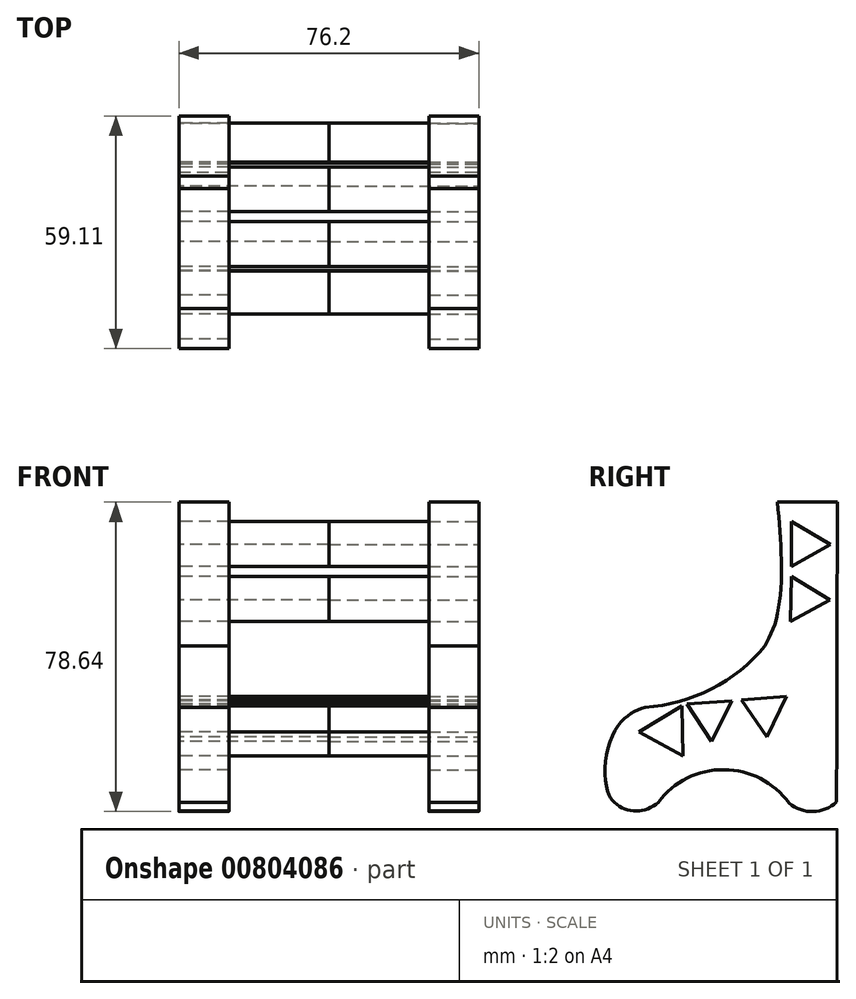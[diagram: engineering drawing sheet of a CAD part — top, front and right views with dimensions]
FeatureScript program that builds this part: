
annotation { "Feature Type Name" : "Feature", "Feature Type Description" : "" }
export const myFeature = defineFeature(function(context is Context, id is Id, definition is map)
    precondition{}
    {
        {
            var Q0;
            Q0=qCreatedBy(makeId("Right.planeOp"),FACE);
            var sketch = newSketch(context, id + "F0", { "sketchPlane" : qUnion([Q0])});
            skArc(sketch, "E0", {"start": v(25.9, -47.46) * mm, "mid": v(31.98, -49.6) * mm, "end": v(37.95, -47.17) * mm});
            skArc(sketch, "E1", {"start": v(-18.5, -47.28) * mm, "mid": v(-12.92, -49.45) * mm, "end": v(-7.36, -47.22) * mm});
            skArc(sketch, "E2", {"start": v(-10.73, -23.11) * mm, "mid": v(6.13, -18.5) * mm, "end": v(19.77, -7.56) * mm});
            skFitSpline(sketch, "E3", {"points": [v(-10.73, -23.11) * mm, v(-13.98, -24.56) * mm, v(-17.73, -28) * mm, v(-20.88, -37.53) * mm, v(-19.91, -45.25) * mm, v(-18.5, -47.28) * mm], "startDerivative": vector(-20.07, -7.67) * mm, "endDerivative": vector(11.02, -12.11) * mm});
            skFitSpline(sketch, "E4", {"points": [v(19.77, -7.56) * mm, v(22.62, -0.69) * mm, v(23.95, 12.57) * mm, v(22.92, 29.03) * mm], "startDerivative": vector(12.21, 23.88) * mm, "endDerivative": vector(-3.87, 42.6) * mm});
            skFitSpline(sketch, "E5", {"points": [v(22.92, 29.03) * mm, v(38.16, 29.03) * mm], "startDerivative": vector(15.37, 0) * mm, "endDerivative": vector(15.37, 0) * mm});
            skFitSpline(sketch, "E6", {"points": [v(38.16, 29.03) * mm, v(37.95, -47.17) * mm], "startDerivative": vector(-0.35, -76.2) * mm, "endDerivative": vector(-0.35, -76.2) * mm});
            skArc(sketch, "E7", {"start": v(25.9, -47.46) * mm, "mid": v(9.33, -38.96) * mm, "end": v(-7.36, -47.22) * mm});
            skSolve(sketch);
        }
        {
            var Q0;
            Q0=makeQuery(id+"F0.imprint","IMPRINT",FACE,{"disambiguationData":[TD([[makeQuery(id+"F0.imprint","IMPRINT",EDGE,{"derivedFrom":sQuery(id+"F0.wireOp",EDGE,"E0")}),1.0]])]});
            var sketch = newSketch(context, id + "F1", { "sketchPlane" : qUnion([Q0])});
            skCircle(sketch, "E8.cCircle", {"center": v(29.76, 18.36) * mm, "radius": 3.3 * mm, "construction": true});
            skLineSegment(sketch, "E8.0", {"start": v(26.42, 12.66) * mm, "end": v(26.5, 24.1) * mm});
            skLineSegment(sketch, "E8.1", {"start": v(26.5, 24.1) * mm, "end": v(36.36, 18.32) * mm});
            skLineSegment(sketch, "E8.2", {"start": v(36.36, 18.32) * mm, "end": v(26.42, 12.66) * mm});
            skPoint(sketch, "E8.0.midPoint", {"position": v(26.46, 18.38) * mm});
            skCircle(sketch, "E9.cCircle", {"center": v(29.65, 4.36) * mm, "radius": 3.3 * mm, "construction": true});
            skLineSegment(sketch, "E9.0", {"start": v(26.5, 10.16) * mm, "end": v(36.25, 4.18) * mm});
            skLineSegment(sketch, "E9.1", {"start": v(36.25, 4.18) * mm, "end": v(26.2, -1.27) * mm});
            skLineSegment(sketch, "E9.2", {"start": v(26.2, -1.27) * mm, "end": v(26.5, 10.16) * mm});
            skPoint(sketch, "E9.0.midPoint", {"position": v(31.38, 7.17) * mm});
            skSolve(sketch);
        }
        {
            var Q0;
            Q0=makeQuery(id+"F1.imprint","IMPRINT",FACE,{"disambiguationData":[TD([[makeQuery(id+"F1.imprint","IMPRINT",EDGE,{"derivedFrom":sQuery(id+"F1.wireOp",EDGE,"E8.0")}),1.0]])]});
            var sketch = newSketch(context, id + "F2", { "sketchPlane" : qUnion([Q0])});
            skCircle(sketch, "E10.cCircle", {"center": v(19.77, -24.05) * mm, "radius": 3.3 * mm, "construction": true});
            skLineSegment(sketch, "E10.0", {"start": v(13.8, -21.23) * mm, "end": v(25.2, -20.3) * mm});
            skLineSegment(sketch, "E10.1", {"start": v(25.2, -20.3) * mm, "end": v(20.3, -30.63) * mm});
            skLineSegment(sketch, "E10.2", {"start": v(20.3, -30.63) * mm, "end": v(13.8, -21.23) * mm});
            skPoint(sketch, "E10.0.midPoint", {"position": v(19.5, -20.76) * mm});
            skCircle(sketch, "E11.cCircle", {"center": v(5.81, -25.16) * mm, "radius": 3.3 * mm, "construction": true});
            skLineSegment(sketch, "E11.0", {"start": v(11.32, -21.52) * mm, "end": v(6.21, -31.75) * mm});
            skLineSegment(sketch, "E11.1", {"start": v(6.21, -31.75) * mm, "end": v(-0.1, -22.22) * mm});
            skLineSegment(sketch, "E11.2", {"start": v(-0.1, -22.22) * mm, "end": v(11.32, -21.52) * mm});
            skPoint(sketch, "E11.0.midPoint", {"position": v(8.77, -26.64) * mm});
            skLineSegment(sketch, "E12.0", {"start": v(13.8, -21.3) * mm, "end": v(25.2, -20.3) * mm, "construction": true});
            skLineSegment(sketch, "E12.1", {"start": v(13.8, -21.3) * mm, "end": v(13.8, -21.23) * mm, "construction": true});
            skLineSegment(sketch, "E12.8", {"start": v(-0.07, -22.52) * mm, "end": v(11.32, -21.52) * mm, "construction": true});
            skLineSegment(sketch, "E12.9", {"start": v(0.27, -31.45) * mm, "end": v(0.4, -31.18) * mm, "construction": true});
            skCircle(sketch, "E13.cCircle", {"center": v(-4.86, -29.18) * mm, "radius": 3.67 * mm, "construction": true});
            skLineSegment(sketch, "E13.0", {"start": v(-12.2, -29.31) * mm, "end": v(-1.3, -22.75) * mm});
            skLineSegment(sketch, "E13.1", {"start": v(-1.3, -22.75) * mm, "end": v(-1.06, -35.47) * mm});
            skLineSegment(sketch, "E13.2", {"start": v(-1.06, -35.47) * mm, "end": v(-12.2, -29.31) * mm});
            skPoint(sketch, "E13.0.midPoint", {"position": v(-6.75, -26.03) * mm});
            skLineSegment(sketch, "E14.0", {"start": v(-12.2, -29.31) * mm, "end": v(-7.51, -32.35) * mm, "construction": true});
            skLineSegment(sketch, "E14.1", {"start": v(-7.51, -32.35) * mm, "end": v(-1.3, -22.75) * mm, "construction": true});
            skSolve(sketch);
        }
        {
            var Q0;
            Q0 = qSketchRegion(id + "F1", true);
            var Q1;
            Q1 = qSketchRegion(id + "F2", true);
            extrude(context, id + "F3", {"entities" : qUnion([Q0, Q1]), "depth" : 38.1 * mm, "offsetDistance" : 25.4 * mm});
        }
        {
            var Q0;
            Q0=makeQuery(id+"F0.imprint","IMPRINT",FACE,{"disambiguationData":[TD([[makeQuery(id+"F0.imprint","IMPRINT",EDGE,{"derivedFrom":sQuery(id+"F0.wireOp",EDGE,"E0")}),1.0]])]});
            extrude(context, id + "F4", {"entities" : qUnion([Q0]), "depth" : 12.7 * mm, "offsetDistance" : 25.4 * mm});
        }
        {
            var Q0;
            Q0=makeQuery(id+"F4.opExtrude","SWEPT_BODY",BODY,{"disambiguationData":[OSD([sQuery(id+"F0.wireOp",EDGE,"E0"),sQuery(id+"F0.wireOp",EDGE,"E1"),sQuery(id+"F0.wireOp",EDGE,"E2"),sQuery(id+"F0.wireOp",EDGE,"E3"),sQuery(id+"F0.wireOp",EDGE,"aa9db85f-fe40-4e03-bcda-879c413f05dc"),sQuery(id+"F0.wireOp",EDGE,"E4"),sQuery(id+"F0.wireOp",EDGE,"E5"),sQuery(id+"F0.wireOp",EDGE,"E6")])]});
            var Q1;
            Q1=makeQuery(id+"F3.opExtrude","SWEPT_BODY",BODY,{"disambiguationData":[OSD([sQuery(id+"F1.wireOp",EDGE,"E8.0"),sQuery(id+"F1.wireOp",EDGE,"E8.1"),sQuery(id+"F1.wireOp",EDGE,"E8.2")])]});
            var Q2;
            Q2=makeQuery(id+"F3.opExtrude","SWEPT_BODY",BODY,{"disambiguationData":[OSD([sQuery(id+"F1.wireOp",EDGE,"E9.0"),sQuery(id+"F1.wireOp",EDGE,"E9.1"),sQuery(id+"F1.wireOp",EDGE,"E9.2")])]});
            var Q3;
            Q3=makeQuery(id+"F3.opExtrude","SWEPT_BODY",BODY,{"disambiguationData":[OSD([sQuery(id+"F2.wireOp",EDGE,"E10.0"),sQuery(id+"F2.wireOp",EDGE,"E10.1"),sQuery(id+"F2.wireOp",EDGE,"E10.2")])]});
            var Q4;
            Q4=makeQuery(id+"F3.opExtrude","SWEPT_BODY",BODY,{"disambiguationData":[OSD([sQuery(id+"F2.wireOp",EDGE,"E11.0"),sQuery(id+"F2.wireOp",EDGE,"E11.1"),sQuery(id+"F2.wireOp",EDGE,"E11.2")])]});
            var Q5;
            Q5=makeQuery(id+"F3.opExtrude","SWEPT_BODY",BODY,{"disambiguationData":[OSD([sQuery(id+"F2.wireOp",EDGE,"E13.0"),sQuery(id+"F2.wireOp",EDGE,"E13.1"),sQuery(id+"F2.wireOp",EDGE,"E13.2")])]});
            var Q6;
            Q6=makeQuery(id+"F3.opExtrude","CAP_FACE",FACE,{"disambiguationData":[OSD([sQuery(id+"F1.wireOp",EDGE,"E8.0"),sQuery(id+"F1.wireOp",EDGE,"E8.1"),sQuery(id+"F1.wireOp",EDGE,"E8.2")])],"isStart":false});
            mirror(context, id + "F5", {"entities" : qUnion([Q0, Q1, Q2, Q3, Q4, Q5]), "mirrorPlane" : qUnion([Q6])});
        }
    });
